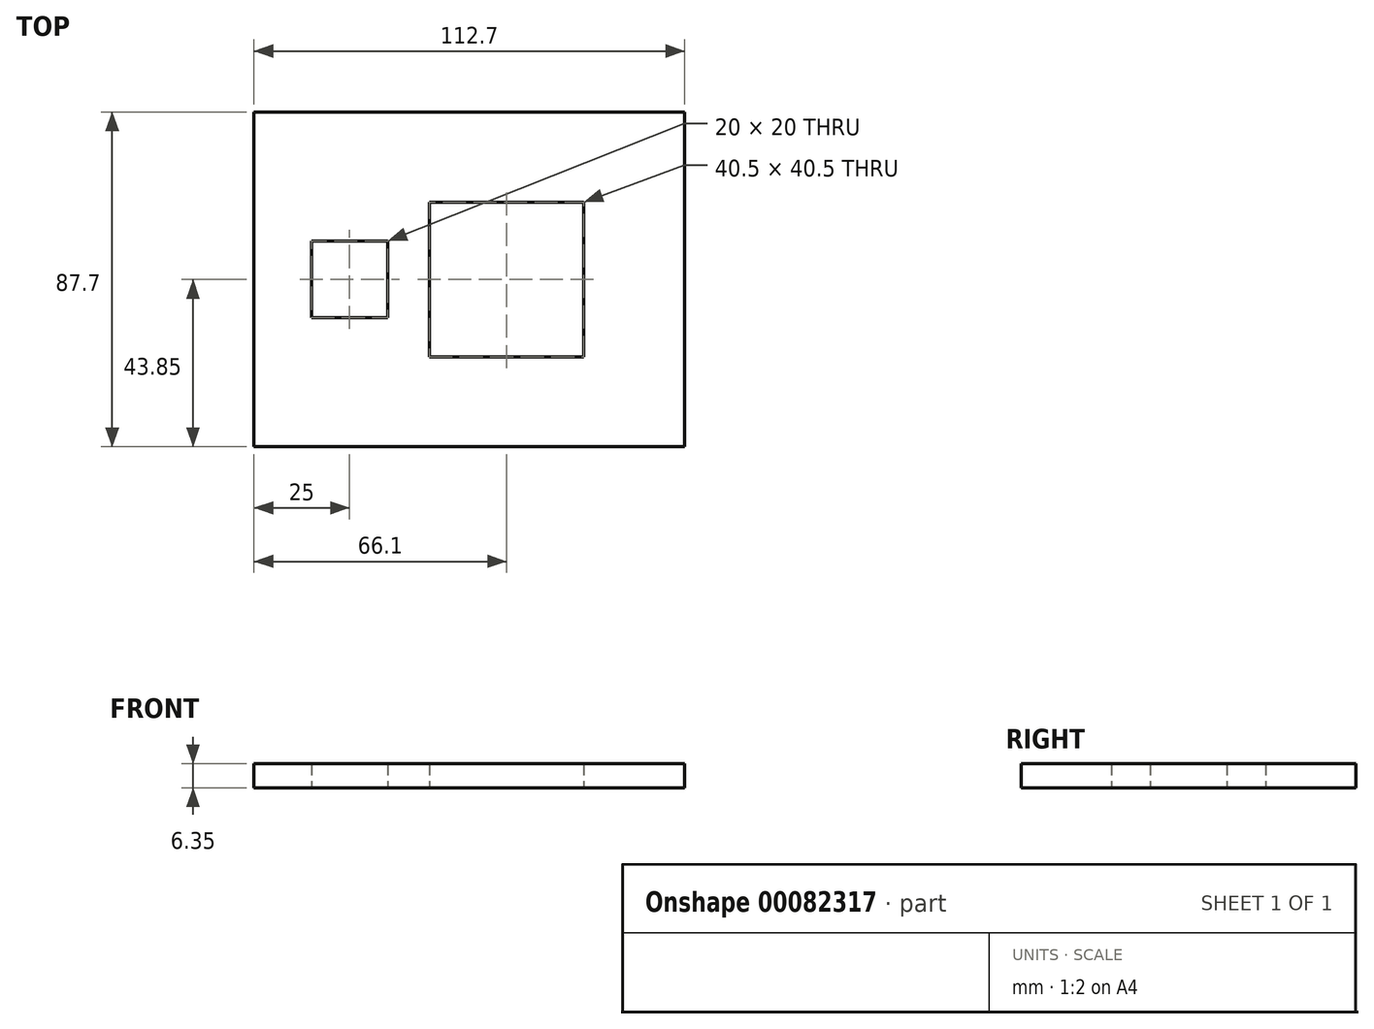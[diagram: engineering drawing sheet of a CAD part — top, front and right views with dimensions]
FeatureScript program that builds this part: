
annotation { "Feature Type Name" : "Feature", "Feature Type Description" : "" }
export const myFeature = defineFeature(function(context is Context, id is Id, definition is map)
    precondition{}
    {
        {
            var Q0;
            Q0=qCreatedBy(makeId("Top.planeOp"),FACE);
            var sketch = newSketch(context, id + "F0", { "sketchPlane" : qUnion([Q0])});
            skLineSegment(sketch, "E0.bottom", {"start": v(50, -37.5) * mm, "end": v(-50, -37.5) * mm});
            skLineSegment(sketch, "E0.top", {"start": v(50, 37.5) * mm, "end": v(-50, 37.5) * mm});
            skLineSegment(sketch, "E0.left", {"start": v(50, -37.5) * mm, "end": v(50, 37.5) * mm});
            skLineSegment(sketch, "E0.right", {"start": v(-50, -37.5) * mm, "end": v(-50, 37.5) * mm});
            skPoint(sketch, "E0.middle", {"position": v(0, 0) * mm});
            skLineSegment(sketch, "E1.bottom", {"start": v(-41.35, 10) * mm, "end": v(-21.35, 10) * mm});
            skLineSegment(sketch, "E1.top", {"start": v(-41.35, -10) * mm, "end": v(-21.35, -10) * mm});
            skLineSegment(sketch, "E1.left", {"start": v(-41.35, 10) * mm, "end": v(-41.35, -10) * mm});
            skLineSegment(sketch, "E1.right", {"start": v(-21.35, 10) * mm, "end": v(-21.35, -10) * mm});
            skLineSegment(sketch, "E2.bottom", {"start": v(30, -20.25) * mm, "end": v(-10.5, -20.25) * mm});
            skLineSegment(sketch, "E2.top", {"start": v(30, 20.25) * mm, "end": v(-10.5, 20.25) * mm});
            skLineSegment(sketch, "E2.left", {"start": v(30, -20.25) * mm, "end": v(30, 20.25) * mm});
            skLineSegment(sketch, "E2.right", {"start": v(-10.5, -20.25) * mm, "end": v(-10.5, 20.25) * mm});
            skPoint(sketch, "E2.middle", {"position": v(9.75, 0) * mm});
            skLineSegment(sketch, "E3", {"start": v(30, -20.25) * mm, "end": v(50, -20.25) * mm});
            skLineSegment(sketch, "E4.bottom", {"start": v(-56.35, 43.85) * mm, "end": v(56.35, 43.85) * mm});
            skLineSegment(sketch, "E4.top", {"start": v(-56.35, -43.85) * mm, "end": v(56.35, -43.85) * mm});
            skLineSegment(sketch, "E4.left", {"start": v(-56.35, 43.85) * mm, "end": v(-56.35, -43.85) * mm});
            skLineSegment(sketch, "E4.right", {"start": v(56.35, 43.85) * mm, "end": v(56.35, -43.85) * mm});
            skLineSegment(sketch, "E5", {"start": v(-50, 37.5) * mm, "end": v(-50, 43.85) * mm});
            skLineSegment(sketch, "E6", {"start": v(-50, 37.5) * mm, "end": v(-56.35, 37.5) * mm});
            skLineSegment(sketch, "E7", {"start": v(50, -37.5) * mm, "end": v(56.35, -37.5) * mm});
            skLineSegment(sketch, "E8", {"start": v(50, -37.5) * mm, "end": v(50, -43.85) * mm});
            skPoint(sketch, "E9", {"position": v(-56.35, 0) * mm});
            skPoint(sketch, "E10", {"position": v(-41.35, 0) * mm});
            skLineSegment(sketch, "E11", {"start": v(-56.35, 0) * mm, "end": v(-41.35, 0) * mm, "construction": true});
            skLineSegment(sketch, "E12", {"start": v(-31.35, 10) * mm, "end": v(-31.35, 43.85) * mm, "construction": true});
            skLineSegment(sketch, "E13", {"start": v(-31.35, -10) * mm, "end": v(-31.35, -43.85) * mm, "construction": true});
            skSolve(sketch);
        }
        {
            var Q0;
            Q0=makeQuery(id+"F0.imprint","IMPRINT",FACE,{"disambiguationData":[TD([[makeQuery(id+"F0.imprint","IMPRINT",EDGE,{"derivedFrom":sQuery(id+"F0.wireOp",EDGE,"E0.bottom")}),-1.0]])]});
            var Q1;
            {var subQ3=sQuery(id+"F0.wireOp",EDGE,"E5");Q1=makeQuery(id+"F0.imprint","IMPRINT",FACE,{"disambiguationData":[TD([[makeQuery(id+"F0.imprint","IMPRINT",EDGE,{"derivedFrom":subQ3}),1.0]])]});}
            var Q2;
            {var subQ5=sQuery(id+"F0.wireOp",EDGE,"E0.top");Q2=makeQuery(id+"F0.imprint","IMPRINT",FACE,{"disambiguationData":[TD([[makeQuery(id+"F0.imprint","IMPRINT",EDGE,{"derivedFrom":subQ5}),-1.0]])]});}
            var Q3;
            Q3=makeQuery(id+"F0.imprint","IMPRINT",FACE,{"disambiguationData":[TD([[makeQuery(id+"F0.imprint","IMPRINT",EDGE,{"derivedFrom":sQuery(id+"F0.wireOp",EDGE,"E0.bottom")}),1.0]])]});
            var Q4;
            {var subQ4=sQuery(id+"F0.wireOp",EDGE,"E7");Q4=makeQuery(id+"F0.imprint","IMPRINT",FACE,{"disambiguationData":[TD([[makeQuery(id+"F0.imprint","IMPRINT",EDGE,{"derivedFrom":subQ4}),-1.0]])]});}
            extrude(context, id + "F1", {"entities" : qUnion([Q0, Q1, Q2, Q3, Q4]), "depth" : 6.35 * mm});
        }
    });
